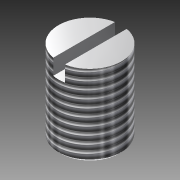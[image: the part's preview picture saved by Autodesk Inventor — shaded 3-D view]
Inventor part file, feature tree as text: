
AUTODESK INVENTOR PART (.ipt)
format: ipt  version: 2013 (Build 170138000, 138)  size: 116,736 bytes
history: native  units: mm (DEFAULTED — no unit token found)
features: extrude x2, sketch x2, chamfer x1, thread x1
ambient origin geometry x8: Origin, YZ Plane, XZ Plane, XY Plane, X Axis, Y Axis, Z Axis, Center Point
bodies: Solid1 (feature_tree)
feature tree (6):
  extrude  "Extrusion1"  Depth=10.3mm TaperAngle=0.0deg
  chamfer  "Chamfer1"  Distance=0.3mm
  thread  "Thread1"  [1 undecoded]
  extrude  "Extrusion2"  Depth=0.75mm
  sketch  "Sketch1"  dims[d0=8.0mm d1=10.3mm d2=0.0mm d3=0.3mm d4=0.3mm d5=10.0mm d6=0.0mm]
  sketch  "Sketch2"  dims[d7=1.5mm d8=0.75mm d9=2.0mm d10=0.0mm d11=45.0deg]
note: 1 required parameter value undecoded (feature->parameter linkage not recoverable at this tier; creation-order binding heuristic only, values carry confidence <= 0.55)
